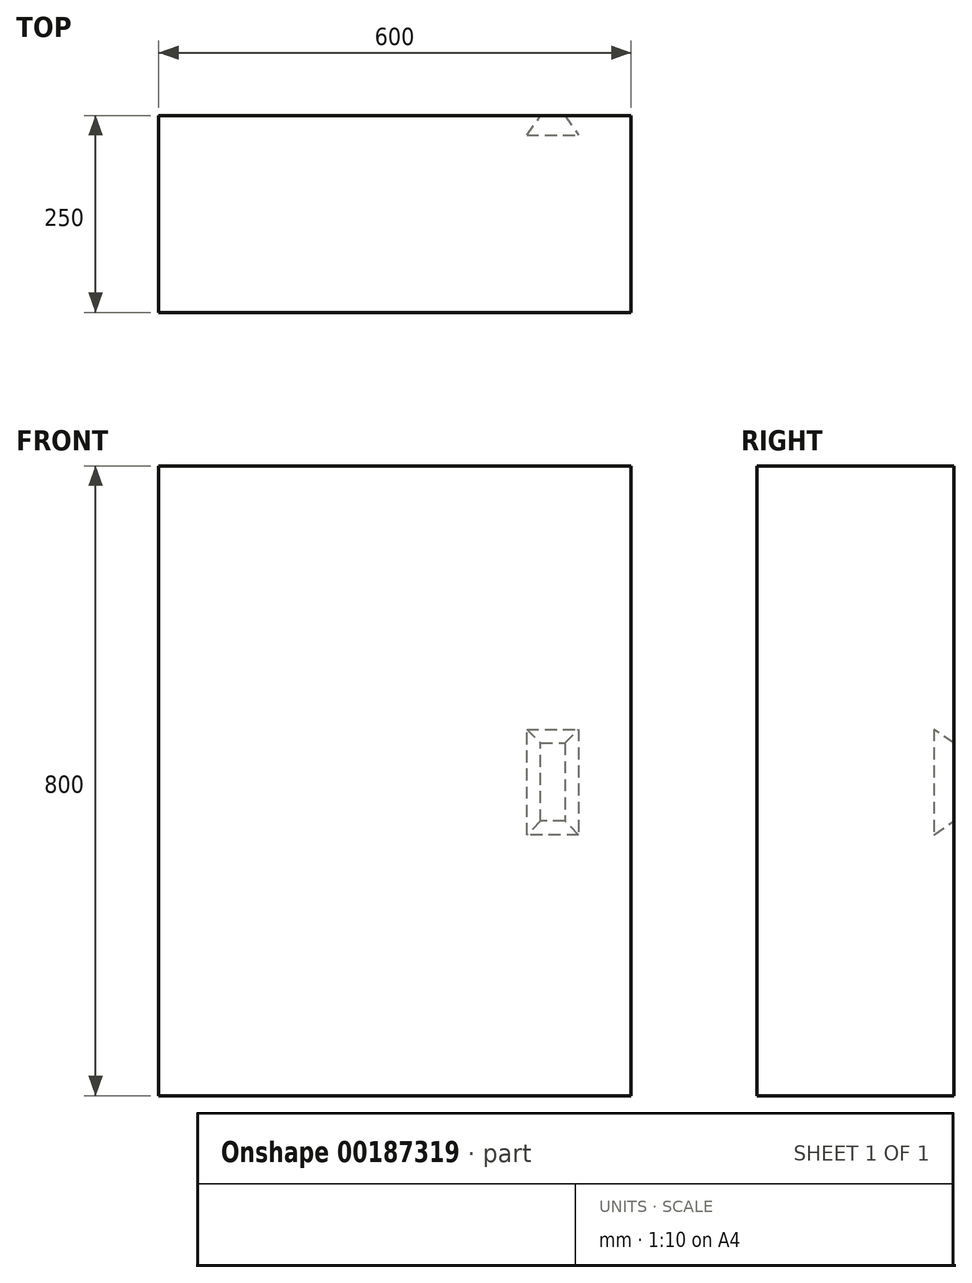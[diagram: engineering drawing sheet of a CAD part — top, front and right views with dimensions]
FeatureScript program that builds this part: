
annotation { "Feature Type Name" : "Feature", "Feature Type Description" : "" }
export const myFeature = defineFeature(function(context is Context, id is Id, definition is map)
    precondition{}
    {
        {
            var Q0;
            Q0=qCreatedBy(makeId("Front.planeOp"),FACE);
            var sketch = newSketch(context, id + "F0", { "sketchPlane" : qUnion([Q0])});
            skLineSegment(sketch, "E0.bottom", {"start": v(300, -400) * mm, "end": v(-300, -400) * mm});
            skLineSegment(sketch, "E0.top", {"start": v(300, 400) * mm, "end": v(-300, 400) * mm});
            skLineSegment(sketch, "E0.left", {"start": v(300, -400) * mm, "end": v(300, 400) * mm});
            skLineSegment(sketch, "E0.right", {"start": v(-300, -400) * mm, "end": v(-300, 400) * mm});
            skPoint(sketch, "E0.middle", {"position": v(0, 0) * mm});
            skSolve(sketch);
        }
        {
            var Q0;
            Q0 = qSketchRegion(id + "F0", true);
            extrude(context, id + "F1", {"entities" : qUnion([Q0]), "depth" : 250 * mm});
        }
        {
            var Q0;
            Q0=makeQuery(id+"F1.opExtrude","CAP_FACE",FACE,{"disambiguationData":[OSD([sQuery(id+"F0.wireOp",EDGE,"E0.bottom"),sQuery(id+"F0.wireOp",EDGE,"E0.top"),sQuery(id+"F0.wireOp",EDGE,"E0.left"),sQuery(id+"F0.wireOp",EDGE,"E0.right")])],"isStart":true});
            var sketch = newSketch(context, id + "F2", { "sketchPlane" : qUnion([Q0])});
            skLineSegment(sketch, "E1.bottom", {"start": v(-216.05, 47.82) * mm, "end": v(-185.3, 47.82) * mm});
            skLineSegment(sketch, "E1.top", {"start": v(-216.05, -51.1) * mm, "end": v(-185.3, -51.1) * mm});
            skLineSegment(sketch, "E1.left", {"start": v(-216.05, 47.82) * mm, "end": v(-216.05, -51.1) * mm});
            skLineSegment(sketch, "E1.right", {"start": v(-185.3, 47.82) * mm, "end": v(-185.3, -51.1) * mm});
            skSolve(sketch);
        }
        {
            var Q0;
            Q0 = qSketchRegion(id + "F2", true);
            extrude(context, id + "F3", {"entities" : qUnion([Q0]), "operationType" : NewBodyOperationType.REMOVE, "oppositeDirection" : true, "depth" : 25 * mm, "hasDraft" : true, "draftAngle" : 35 * degree});
        }
    });
